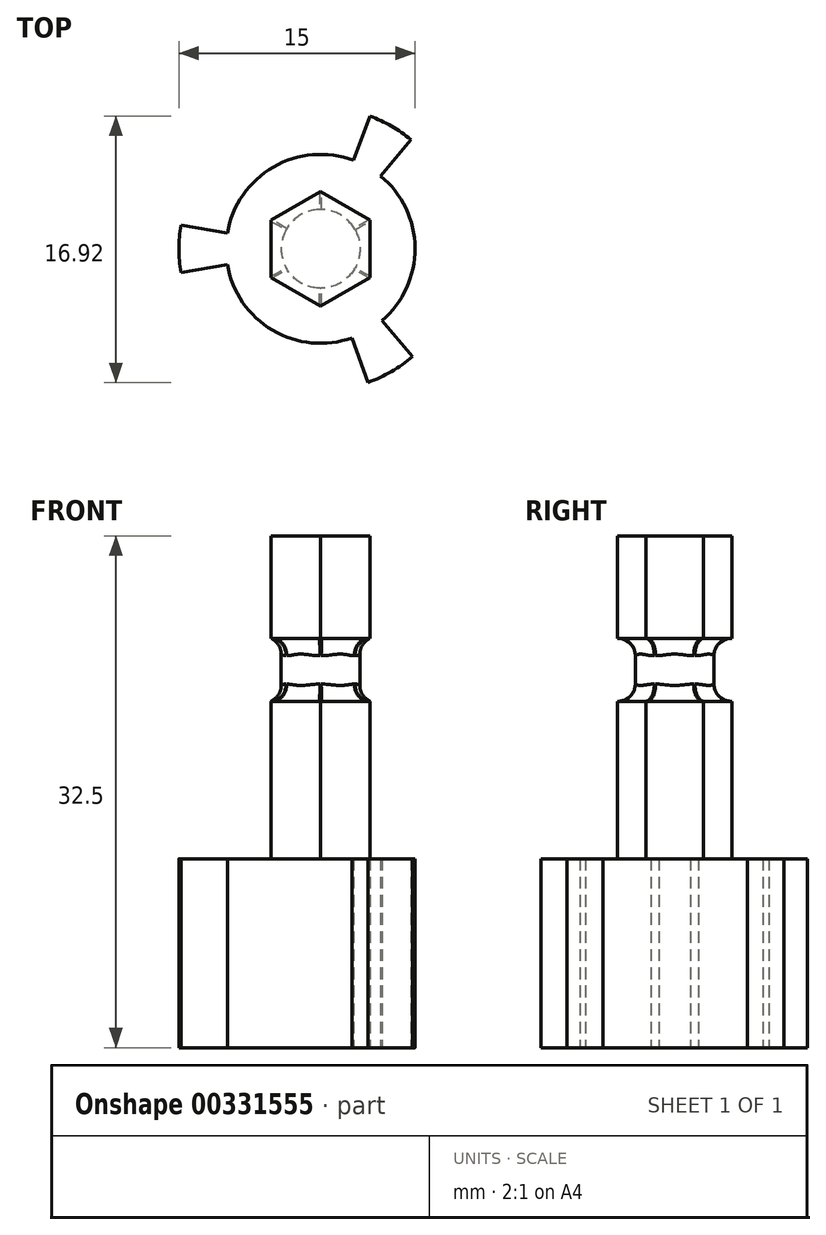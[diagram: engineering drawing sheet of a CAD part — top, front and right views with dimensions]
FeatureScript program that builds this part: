
annotation { "Feature Type Name" : "Feature", "Feature Type Description" : "" }
export const myFeature = defineFeature(function(context is Context, id is Id, definition is map)
    precondition{}
    {
        {
            var Q0;
            Q0=qCreatedBy(makeId("Top.planeOp"),FACE);
            var sketch = newSketch(context, id + "F0", { "sketchPlane" : qUnion([Q0])});
            skCircle(sketch, "E0", {"center": v(0, 0) * mm, "radius": 9 * mm});
            skCircle(sketch, "E1.cCircle", {"center": v(0, 0) * mm, "radius": 9 * mm, "construction": true});
            skLineSegment(sketch, "E1.0", {"start": v(-9, 0) * mm, "end": v(4.5, 7.8) * mm, "construction": true});
            skLineSegment(sketch, "E1.1", {"start": v(4.5, 7.8) * mm, "end": v(4.5, -7.8) * mm, "construction": true});
            skLineSegment(sketch, "E1.2", {"start": v(4.5, -7.8) * mm, "end": v(-9, 0) * mm, "construction": true});
            skCircle(sketch, "E2", {"center": v(0, 0) * mm, "radius": 6 * mm});
            skPoint(sketch, "E3", {"position": v(-8.87, 1.5) * mm});
            skPoint(sketch, "E4", {"position": v(-8.87, -1.5) * mm});
            skLineSegment(sketch, "E5", {"start": v(-8.87, 1.5) * mm, "end": v(-5.92, 1) * mm});
            skLineSegment(sketch, "E6", {"start": v(-8.87, -1.5) * mm, "end": v(-5.92, -1) * mm});
            skPoint(sketch, "E7", {"position": v(3.14, 8.43) * mm});
            skPoint(sketch, "E8", {"position": v(5.73, 6.94) * mm});
            skPoint(sketch, "E9", {"position": v(5.85, -6.84) * mm});
            skPoint(sketch, "E10", {"position": v(3, -8.49) * mm});
            skLineSegment(sketch, "E11", {"start": v(4.5, 7.8) * mm, "end": v(0, 0) * mm, "construction": true});
            skLineSegment(sketch, "E12", {"start": v(4.5, -7.8) * mm, "end": v(0, 0) * mm, "construction": true});
            skLineSegment(sketch, "E13", {"start": v(3.14, 8.43) * mm, "end": v(2.1, 5.62) * mm});
            skLineSegment(sketch, "E14", {"start": v(5.73, 6.94) * mm, "end": v(3.82, 4.63) * mm});
            skLineSegment(sketch, "E15", {"start": v(5.85, -6.84) * mm, "end": v(3.9, -4.56) * mm});
            skLineSegment(sketch, "E16", {"start": v(3, -8.49) * mm, "end": v(2, -5.66) * mm});
            skSolve(sketch);
        }
        {
            var Q0;
            {var subQ0=sQuery(id+"F0.wireOp",EDGE,"E5");Q0=makeQuery(id+"F0.imprint","IMPRINT",FACE,{"disambiguationData":[TD([[makeQuery(id+"F0.imprint","IMPRINT",EDGE,{"derivedFrom":subQ0}),-1.0]])]});}
            var Q1;
            {var subQ0=sQuery(id+"F0.wireOp",EDGE,"E2");var subQ4=makeQuery(id+"F0.imprint","INTERSECT",VERTEX,{"derivedFrom":[subQ0,sQuery(id+"F0.wireOp",EDGE,"E13")]});Q1=makeQuery(id+"F0.imprint","IMPRINT",FACE,{"disambiguationData":[TD([[makeQuery(id+"F0.imprint","IMPRINT",EDGE,{"disambiguationData":[TD([[subQ4,1.0]])],"derivedFrom":subQ0}),1.0]])]});}
            var Q2;
            {var subQ0=sQuery(id+"F0.wireOp",EDGE,"E13");Q2=makeQuery(id+"F0.imprint","IMPRINT",FACE,{"disambiguationData":[TD([[makeQuery(id+"F0.imprint","IMPRINT",EDGE,{"derivedFrom":subQ0}),1.0]])]});}
            var Q3;
            {var subQ0=sQuery(id+"F0.wireOp",EDGE,"E15");Q3=makeQuery(id+"F0.imprint","IMPRINT",FACE,{"disambiguationData":[TD([[makeQuery(id+"F0.imprint","IMPRINT",EDGE,{"derivedFrom":subQ0}),1.0]])]});}
            extrude(context, id + "F1", {"entities" : qUnion([Q0, Q1, Q2, Q3]), "depth" : 12 * mm});
        }
        {
            var Q0;
            Q0=makeQuery(id+"F1.opExtrude","CAP_FACE",FACE,{"disambiguationData":[OSD([sQuery(id+"F0.wireOp",EDGE,"E0"),sQuery(id+"F0.wireOp",EDGE,"E2"),sQuery(id+"F0.wireOp",EDGE,"E5"),sQuery(id+"F0.wireOp",EDGE,"E6"),sQuery(id+"F0.wireOp",EDGE,"E13"),sQuery(id+"F0.wireOp",EDGE,"E14"),sQuery(id+"F0.wireOp",EDGE,"E15"),sQuery(id+"F0.wireOp",EDGE,"E16")])],"isStart":false});
            var sketch = newSketch(context, id + "F2", { "sketchPlane" : qUnion([Q0])});
            skCircle(sketch, "E17", {"center": v(0, 0) * mm, "radius": 3.15 * mm});
            skCircle(sketch, "E18.cCircle", {"center": v(0, 0) * mm, "radius": 3.15 * mm, "construction": true});
            skLineSegment(sketch, "E18.0", {"start": v(-3.15, -1.82) * mm, "end": v(-3.15, 1.82) * mm});
            skLineSegment(sketch, "E18.1", {"start": v(-3.15, 1.82) * mm, "end": v(0, 3.64) * mm});
            skLineSegment(sketch, "E18.2", {"start": v(0, 3.64) * mm, "end": v(3.15, 1.82) * mm});
            skLineSegment(sketch, "E18.3", {"start": v(3.15, 1.82) * mm, "end": v(3.15, -1.82) * mm});
            skLineSegment(sketch, "E18.4", {"start": v(3.15, -1.82) * mm, "end": v(0, -3.64) * mm});
            skLineSegment(sketch, "E18.5", {"start": v(0, -3.64) * mm, "end": v(-3.15, -1.82) * mm});
            skPoint(sketch, "E18.0.midPoint", {"position": v(-3.15, 0) * mm});
            skSolve(sketch);
        }
        {
            var Q0;
            Q0 = qSketchRegion(id + "F2", true);
            extrude(context, id + "F3", {"entities" : qUnion([Q0]), "operationType" : NewBodyOperationType.ADD, "depth" : 10 * mm});
        }
        {
            var Q0;
            Q0=makeQuery(id+"F3.opExtrude","CAP_FACE",FACE,{"disambiguationData":[OSD([sQuery(id+"F2.wireOp",EDGE,"E18.0"),sQuery(id+"F2.wireOp",EDGE,"E18.1"),sQuery(id+"F2.wireOp",EDGE,"E18.2"),sQuery(id+"F2.wireOp",EDGE,"E18.3"),sQuery(id+"F2.wireOp",EDGE,"E18.4"),sQuery(id+"F2.wireOp",EDGE,"E18.5")])],"isStart":false});
            var sketch = newSketch(context, id + "F4", { "sketchPlane" : qUnion([Q0])});
            skCircle(sketch, "E19", {"center": v(0, 0) * mm, "radius": 2.5 * mm});
            skSolve(sketch);
        }
        {
            var Q0;
            Q0 = qSketchRegion(id + "F4", true);
            extrude(context, id + "F5", {"entities" : qUnion([Q0]), "operationType" : NewBodyOperationType.ADD, "depth" : 4 * mm});
        }
        {
            var Q0;
            Q0=makeQuery(id+"F5.opExtrude","CAP_FACE",FACE,{"disambiguationData":[OSD([sQuery(id+"F4.wireOp",EDGE,"E19")])],"isStart":false});
            var sketch = newSketch(context, id + "F6", { "sketchPlane" : qUnion([Q0])});
            skCircle(sketch, "E20.cCircle", {"center": v(0, 0) * mm, "radius": 3.15 * mm, "construction": true});
            skLineSegment(sketch, "E20.0", {"start": v(-3.15, -1.82) * mm, "end": v(-3.15, 1.82) * mm});
            skLineSegment(sketch, "E20.1", {"start": v(-3.15, 1.82) * mm, "end": v(0, 3.64) * mm});
            skLineSegment(sketch, "E20.2", {"start": v(0, 3.64) * mm, "end": v(3.15, 1.82) * mm});
            skLineSegment(sketch, "E20.3", {"start": v(3.15, 1.82) * mm, "end": v(3.15, -1.82) * mm});
            skLineSegment(sketch, "E20.4", {"start": v(3.15, -1.82) * mm, "end": v(0, -3.64) * mm});
            skLineSegment(sketch, "E20.5", {"start": v(0, -3.64) * mm, "end": v(-3.15, -1.82) * mm});
            skPoint(sketch, "E20.0.midPoint", {"position": v(-3.15, 0) * mm});
            skSolve(sketch);
        }
        {
            var Q0;
            Q0 = qSketchRegion(id + "F6", true);
            extrude(context, id + "F7", {"entities" : qUnion([Q0]), "operationType" : NewBodyOperationType.ADD, "depth" : 6.5 * mm});
        }
        {
            var Q0;
            Q0=makeQuery(id+"F5.opExtrude","SWEPT_FACE",FACE,{"disambiguationData":[OSD([sQuery(id+"F4.wireOp",EDGE,"E19")])]});
            fillet(context, id + "F8", {"entities" : qUnion([Q0]), "radius" : 1.1 * mm, "tangentPropagation" : true, "allowEdgeOverflow" : false});
        }
    });
